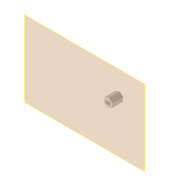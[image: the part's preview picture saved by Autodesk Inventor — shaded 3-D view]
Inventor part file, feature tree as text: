
AUTODESK INVENTOR PART (.ipt)
format: ipt  version: 2022 (Build 260153000, 153)  size: 91,648 bytes
history: native  units: mm
features: reference x8, other x6, plane x1, extrude x1, sketch x1
ambient origin geometry x8: Origin, YZ Plane, XZ Plane, XY Plane, X Axis, Y Axis, Z Axis, Center Point
bodies: Volumenkörper1 (feature_tree)
feature tree (17):
  plane  "Arbeitsebene1"
  extrude  "Extrusion1"  Depth=10.0mm TaperAngle=0.0deg
  sketch  "Skizze1"  dims[d0=0.2mm d1=10.0mm d2=0.0mm d3=0.1mm]
  reference  "Referenz1"
  reference  "Referenz2"
  reference  "Referenz3"
  reference  "Referenz4"
  reference  "Referenz5"
  reference  "Referenz6"
  reference  "Referenz7"
  reference  "Referenz8"
  other  "Assembly_Cassete_Deck.iam"
  other  "00_Cassette:1"
  parser-record x3  (decoder bookkeeping rows leaked as tree rows — omitted from the tree; the rows remain in map.json)
  other  "00_Stepper_Motor_28BYJ-48:1"
